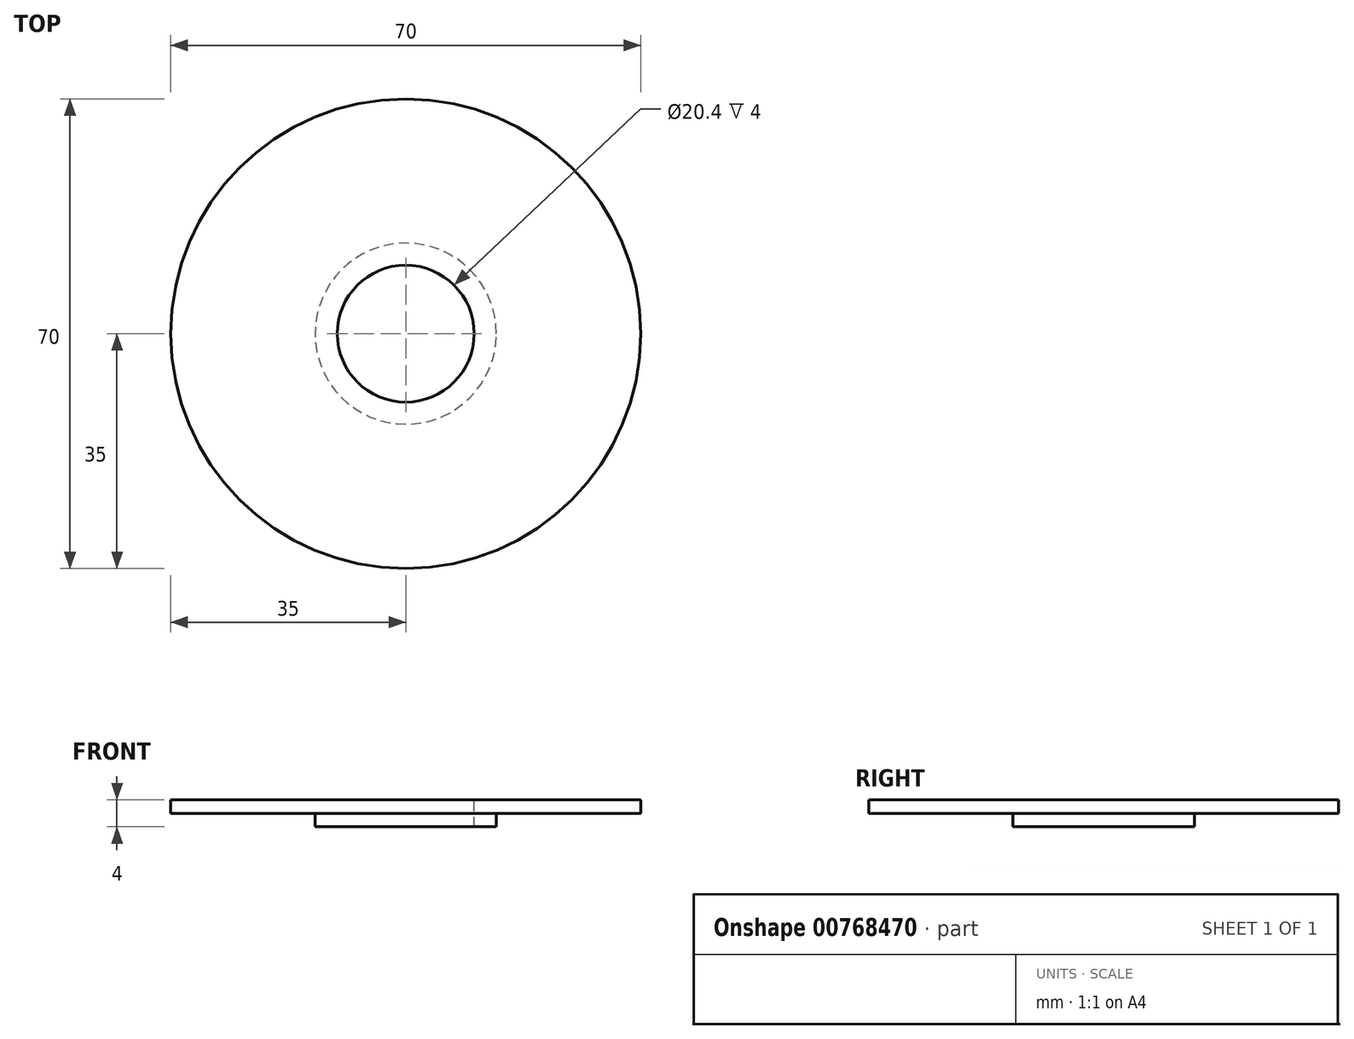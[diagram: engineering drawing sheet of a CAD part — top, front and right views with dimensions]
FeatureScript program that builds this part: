
annotation { "Feature Type Name" : "Feature", "Feature Type Description" : "" }
export const myFeature = defineFeature(function(context is Context, id is Id, definition is map)
    precondition{}
    {
        {
            var Q0;
            Q0=qCreatedBy(makeId("Top.planeOp"),FACE);
            var sketch = newSketch(context, id + "F0", { "sketchPlane" : qUnion([Q0])});
            skCircle(sketch, "E0", {"center": v(0, 0) * mm, "radius": 10 * mm});
            skCircle(sketch, "E1", {"center": v(-50, 0) * mm, "radius": 10 * mm});
            skLineSegment(sketch, "E2", {"start": v(-50, 0) * mm, "end": v(0, 0) * mm});
            skLineSegment(sketch, "E3.bottom", {"start": v(-70, 20) * mm, "end": v(20, 20) * mm});
            skLineSegment(sketch, "E3.top", {"start": v(-70, -20) * mm, "end": v(20, -20) * mm});
            skLineSegment(sketch, "E3.left", {"start": v(-70, 20) * mm, "end": v(-70, -20) * mm});
            skLineSegment(sketch, "E3.right", {"start": v(20, 20) * mm, "end": v(20, -20) * mm});
            skPoint(sketch, "E3.middle", {"position": v(-25, 0) * mm});
            skCircle(sketch, "E4", {"center": v(0, 0) * mm, "radius": 35 * mm});
            skSolve(sketch);
        }
        {
            var Q0;
            {var subQ0=sQuery(id+"F0.wireOp",EDGE,"E3.right");Q0=makeQuery(id+"F0.imprint","IMPRINT",FACE,{"disambiguationData":[TD([[makeQuery(id+"F0.imprint","IMPRINT",EDGE,{"derivedFrom":subQ0}),1.0]])]});}
            var Q1;
            Q1=makeQuery(id+"F0.imprint","IMPRINT",FACE,{"disambiguationData":[TD([[makeQuery(id+"F0.imprint","IMPRINT",EDGE,{"derivedFrom":sQuery(id+"F0.wireOp",EDGE,"E0")}),-1.0]])]});
            extrude(context, id + "F1", {"entities" : qUnion([Q0, Q1]), "depth" : 3 * mm, "offsetDistance" : 25 * mm});
        }
        {
            var Q0;
            Q0=makeQuery(id+"F1.opExtrude","CAP_FACE",FACE,{"disambiguationData":[OSD([sQuery(id+"F0.wireOp",EDGE,"E0"),sQuery(id+"F0.wireOp",EDGE,"E4")])],"isStart":true});
            var sketch = newSketch(context, id + "F2", { "sketchPlane" : qUnion([Q0])});
            skCircle(sketch, "E5", {"center": v(0, 0) * mm, "radius": 13.5 * mm});
            skSolve(sketch);
        }
        {
            var Q0;
            Q0=makeQuery(id+"F2.imprint","IMPRINT",FACE,{"disambiguationData":[TD([[makeQuery(id+"F2.imprint","IMPRINT",EDGE,{"derivedFrom":sQuery(id+"F2.wireOp",EDGE,"E5")}),1.0]])]});
            extrude(context, id + "F3", {"entities" : qUnion([Q0]), "operationType" : NewBodyOperationType.ADD, "depth" : 2 * mm, "offsetDistance" : 25 * mm});
        }
        {
            var Q0;
            Q0=makeQuery(id+"F1.opExtrude","CAP_FACE",FACE,{"disambiguationData":[OSD([sQuery(id+"F0.wireOp",EDGE,"E0"),sQuery(id+"F0.wireOp",EDGE,"E4")])],"isStart":false});
            extrude(context, id + "F4", {"entities" : qUnion([Q0]), "operationType" : NewBodyOperationType.REMOVE, "oppositeDirection" : true, "depth" : 1 * mm, "offsetDistance" : 25 * mm});
        }
        {
            var Q0;
            Q0=makeQuery(id+"F4.boolean.opBoolean","COPY",FACE,{"derivedFrom":makeQuery(id+"F4.opExtrude","CAP_FACE",FACE,{"disambiguationData":[OSD([sQuery(id+"F0.wireOp",EDGE,"E0"),sQuery(id+"F0.wireOp",EDGE,"E4")])],"isStart":false})});
            var sketch = newSketch(context, id + "F5", { "sketchPlane" : qUnion([Q0])});
            skCircle(sketch, "E6", {"center": v(0, 0) * mm, "radius": 10.2 * mm});
            skSolve(sketch);
        }
        {
            var Q0;
            Q0=makeQuery(id+"F5.imprint","IMPRINT",FACE,{"disambiguationData":[TD([[makeQuery(id+"F5.imprint","IMPRINT",EDGE,{"derivedFrom":sQuery(id+"F5.wireOp",EDGE,"E6")}),1.0]])]});
            extrude(context, id + "F6", {"entities" : qUnion([Q0]), "operationType" : NewBodyOperationType.REMOVE, "oppositeDirection" : true, "depth" : 25 * mm, "offsetDistance" : 25 * mm});
        }
    });
